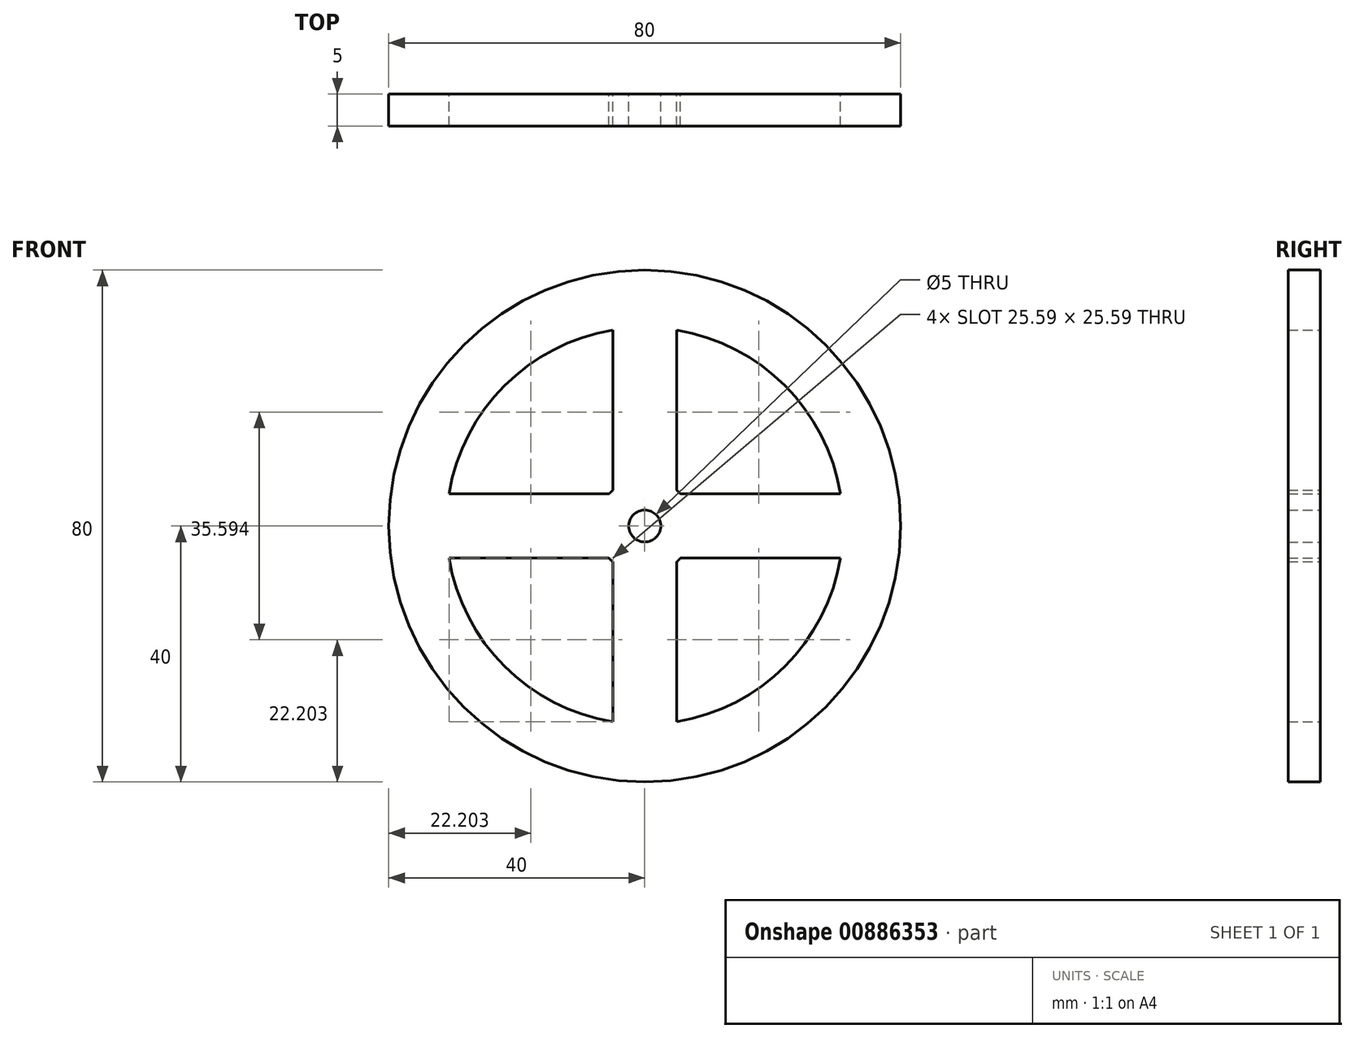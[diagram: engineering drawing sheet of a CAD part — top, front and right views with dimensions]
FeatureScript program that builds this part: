
annotation { "Feature Type Name" : "Feature", "Feature Type Description" : "" }
export const myFeature = defineFeature(function(context is Context, id is Id, definition is map)
    precondition{}
    {
        {
            var Q0;
            Q0=qCreatedBy(makeId("Front.planeOp"),FACE);
            var sketch = newSketch(context, id + "F0", { "sketchPlane" : qUnion([Q0])});
            skCircle(sketch, "E0", {"center": v(0, 0) * mm, "radius": 40 * mm});
            skArc(sketch, "E1", {"start": v(30.6, 5) * mm, "mid": v(21.92, 21.92) * mm, "end": v(5, 30.6) * mm});
            skArc(sketch, "E2", {"start": v(-5.6, -5) * mm, "mid": v(-5.3, -5.3) * mm, "end": v(-5, -5.6) * mm});
            skCircle(sketch, "E3", {"center": v(0, 0) * mm, "radius": 2.5 * mm});
            skLineSegment(sketch, "E4", {"start": v(0, 0) * mm, "end": v(0, 31) * mm, "construction": true});
            skLineSegment(sketch, "E5", {"start": v(0, 0) * mm, "end": v(31, 0) * mm, "construction": true});
            skLineSegment(sketch, "E6", {"start": v(0, 0) * mm, "end": v(0, -31) * mm, "construction": true});
            skLineSegment(sketch, "E7", {"start": v(0, 0) * mm, "end": v(-31, 0) * mm, "construction": true});
            skLineSegment(sketch, "E8.0", {"start": v(-5, 5.6) * mm, "end": v(-5, 30.6) * mm});
            skLineSegment(sketch, "E9.0", {"start": v(5, 5.6) * mm, "end": v(5, 30.6) * mm});
            skLineSegment(sketch, "E10.0", {"start": v(-5.6, -5) * mm, "end": v(-30.6, -5) * mm});
            skLineSegment(sketch, "E11.0", {"start": v(-5.6, 5) * mm, "end": v(-30.6, 5) * mm});
            skLineSegment(sketch, "E12.0", {"start": v(-5, -5.6) * mm, "end": v(-5, -30.6) * mm});
            skLineSegment(sketch, "E13.0", {"start": v(5, -5.6) * mm, "end": v(5, -30.6) * mm});
            skLineSegment(sketch, "E14.0", {"start": v(5.6, -5) * mm, "end": v(30.6, -5) * mm});
            skLineSegment(sketch, "E15.0", {"start": v(5.6, 5) * mm, "end": v(30.6, 5) * mm});
            skArc(sketch, "E16.trimOffspring", {"start": v(-5, 30.6) * mm, "mid": v(-21.92, 21.92) * mm, "end": v(-30.6, 5) * mm});
            skArc(sketch, "E17.trimOffspring", {"start": v(5, -30.6) * mm, "mid": v(21.92, -21.92) * mm, "end": v(30.6, -5) * mm});
            skArc(sketch, "E18.trimOffspring", {"start": v(-30.6, -5) * mm, "mid": v(-21.92, -21.92) * mm, "end": v(-5, -30.6) * mm});
            skArc(sketch, "E19.trimOffspring", {"start": v(5, -5.6) * mm, "mid": v(5.3, -5.3) * mm, "end": v(5.6, -5) * mm});
            skArc(sketch, "E20.trimOffspring", {"start": v(5.6, 5) * mm, "mid": v(5.3, 5.3) * mm, "end": v(5, 5.6) * mm});
            skArc(sketch, "E21.trimOffspring", {"start": v(-5, 5.6) * mm, "mid": v(-5.3, 5.3) * mm, "end": v(-5.6, 5) * mm});
            skSolve(sketch);
        }
        {
            var Q0;
            Q0=makeQuery(id+"F0.imprint","IMPRINT",FACE,{"disambiguationData":[TD([[makeQuery(id+"F0.imprint","IMPRINT",EDGE,{"derivedFrom":sQuery(id+"F0.wireOp",EDGE,"E0")}),1.0]])]});
            extrude(context, id + "F1", {"entities" : qUnion([Q0]), "endBound" : BoundingType.SYMMETRIC, "depth" : 5 * mm, "offsetDistance" : 25 * mm});
        }
    });
